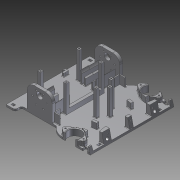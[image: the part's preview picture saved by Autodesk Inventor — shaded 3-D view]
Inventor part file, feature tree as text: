
AUTODESK INVENTOR PART (.ipt)
format: ipt  version: 2011 SP2 (Build 150309200, 309)  size: 1,286,144 bytes
history: native  units: mm
features: extrude x37, sketch x23, projected_geometry x15, fillet x14, mirror x3, plane x1, chamfer x1, hole x1
ambient origin geometry x8: Origin, YZ Plane, XZ Plane, XY Plane, X Axis, Y Axis, Z Axis, Center Point
feature tree (95):
  sketch  "Sketch1"  dims[d0=200.0mm d1=200.0mm]
  extrude  "Extrusion3"  Depth=200.0mm
  extrude  "Extrusion4"  Depth=10.5mm
  extrude  "Extrusion5"  Depth=6.5mm
  extrude  "Extrusion6"  Depth=53.3mm
  extrude  "Extrusion7"  Depth=26.65mm
  sketch  "Sketch4"  dims[d6=6.5mm d8=53.3mm]
  extrude  "Extrusion8"  Depth=5.0mm
  extrude  "Extrusion9"  Depth=5.0mm
  extrude  "Extrusion10"  Depth=4.6mm
  plane  "Work Plane1"
  mirror  "Mirror1"
  sketch  "Sketch9"  dims[d9=53.3mm d10=26.65mm]
  sketch  "Sketch10"  dims[d11=26.65mm d13=5.0mm]
  extrude  "Extrusion16"  Depth=8.0mm
  extrude  "Extrusion17"  Depth=8.0mm
  extrude  "Extrusion18"  Depth=138.0mm
  extrude  "Extrusion19"  Depth=3.0mm
  extrude  "Extrusion20"  Depth=12.061mm
  extrude  "Extrusion21"  Depth=4.0mm TaperAngle=0.0deg
  extrude  "Extrusion22"  Depth=55.0mm TaperAngle=0.0deg
  sketch  "Sketch13"  dims[d18=4.6mm d19=8.0mm]
  extrude  "Extrusion26"  Depth=38.0mm
  extrude  "Extrusion27"  Depth=7.0mm
  extrude  "Extrusion30"  Depth=15.5mm
  extrude  "Extrusion32"  Depth=55.0mm TaperAngle=0.0deg
  extrude  "Extrusion33"  Depth=2.0mm
  extrude  "Extrusion34"  Depth=3.9mm
  chamfer  "Chamfer2"  Distance=55.0mm
  fillet  "Fillet1"  Radius=36.8mm
  extrude  "Extrusion35"  Depth=40.0mm TaperAngle=0.0deg
  extrude  "Extrusion36"  Depth=23.0mm TaperAngle=0.0deg
  sketch  "Sketch21"  dims[d41=6.6mm d42=1.5mm d49=12.061mm]
  extrude  "Extrusion37"  Depth=2.8mm
  extrude  "Extrusion39"  Depth=2.8mm
  extrude  "Extrusion40"  Depth=2.8mm
  fillet  "Fillet2"  Radius=2.8mm
  sketch  "Sketch28"  dims[d64=13.0mm d65=38.0mm]
  extrude  "Extrusion48"  Depth=32.757mm
  extrude  "Extrusion49"  Depth=32.757mm
  extrude  "Extrusion42"  Depth=80.957mm
  extrude  "Extrusion44"  Depth=80.957mm
  fillet  "Fillet4"  Radius=27.264mm
  mirror  "Mirror3"
  fillet  "Fillet3"  Radius=20.564mm
  extrude  "Extrusion45"  Depth=34.936mm
  sketch  "Sketch30"  dims[d68=3.0mm d69=15.5mm]
  extrude  "Extrusion46"  Depth=35.936mm
  extrude  "Extrusion47"  Depth=2.0mm
  hole  "Hole1"  [1 undecoded]
  fillet  "Fillet5"  Radius=11.0mm
  fillet  "Fillet6"  Radius=2.0mm
  fillet  "Fillet7"  Radius=11.0mm
  fillet  "Fillet8"  Radius=11.0mm
  fillet  "Fillet9"  Radius=2.0mm
  fillet  "Fillet10"  Radius=2.0mm
  fillet  "Fillet11"  Radius=6.0mm
  fillet  "Fillet12"  Radius=6.0mm
  extrude  "Extrusion50"  Depth=6.0mm
  extrude  "Extrusion51"  Depth=6.0mm
  extrude  "Extrusion52"  Depth=3.0mm
  fillet  "Fillet13"  Radius=3.0mm
  fillet  "Fillet14"  Radius=3.0mm
  extrude  "Extrusion53"  Depth=3.0mm
  mirror  "Mirror4"
  sketch  "Sketch2"  dims[d2=10.5mm d3=10.5mm]
  sketch  "Sketch3"  dims[d4=57.861mm d5=6.5mm]
  projected_geometry  "Projected Loop1"
  projected_geometry  "Projected Loop7"
  sketch  "Sketch11"  dims[d14=5.0mm d15=5.0mm]
  sketch  "Sketch12"  dims[d16=6.35mm d17=4.6mm]
  projected_geometry  "Projected Loop8"
  sketch  "Sketch15"  dims[d20=5.0mm d21=8.0mm]
  projected_geometry  "Projected Loop9"
  sketch  "Sketch18"  dims[d22=5.0mm d25=138.0mm]
  projected_geometry  "Projected Loop11"
  sketch  "Sketch20"  dims[d29=3.65mm d30=3.65mm d31=3.0mm d34=1.5mm d37=3.0mm d38=5.0mm]
  projected_geometry  "Projected Loop12"
  sketch  "Sketch25"  dims[d50=5.0mm d58=4.0mm d59=0.0mm]
  sketch  "Sketch27"  dims[d60=11.0mm d61=0.0mm d62=55.0mm d63=0.0mm]
  projected_geometry  "Projected Loop16"
  sketch  "Sketch29"  dims[d66=36.8mm d67=7.0mm]
  sketch  "Sketch31"  dims[d70=60.0mm d72=360.0deg d74=55.0mm d75=0.0mm]
  projected_geometry  "Projected Loop17"
  projected_geometry  "Projected Loop18"
  projected_geometry  "Projected Loop19"
  projected_geometry  "Projected Loop20"
  projected_geometry  "Projected Loop21"
  projected_geometry  "Projected Loop22"
  projected_geometry  "Projected Loop23"
  sketch  "Sketch32"  dims[d76=2.0mm d77=2.0mm]
  sketch  "Sketch33"  dims[d78=3.9mm d79=3.9mm d80=55.0mm d81=0.0mm d82=36.8mm]
  sketch  "Sketch34"  dims[d83=36.0mm d84=40.0mm d85=0.0mm]
  sketch  "Sketch35"  dims[d86=40.0mm d87=0.0mm d88=23.0mm d89=0.0mm d119=2.8mm d120=2.8mm d121=2.8mm d122=2.8mm d135=32.757mm d136=32.757mm d137=80.957mm d138=80.957mm d139=27.264mm d140=20.564mm d141=34.936mm d142=35.936mm d143=2.0mm d144=11.0mm d145=11.0mm d146=2.0mm d147=11.0mm d148=11.0mm d149=2.0mm d150=2.0mm d155=6.0mm d156=6.0mm d157=6.0mm d158=6.0mm d159=3.0mm d160=3.0mm d161=3.0mm d162=3.0mm d163=6.0mm d164=6.0mm d165=3.0mm d166=3.0mm d167=6.0mm d168=6.0mm d169=3.0mm d170=3.0mm d181=3.0mm d182=3.5mm d184=0.0mm d185=0.0mm d186=200.0mm d187=0.0mm d188=200.0mm d189=0.0mm d190=58.0mm d191=0.0mm d192=18.0mm d193=0.0mm d194=40.0mm d195=0.0mm d196=1.570796mm d197=1.570796mm d198=220.0mm d199=220.0mm d200=10.0mm d201=10.0mm d202=5.0mm d203=7.0mm d204=0.0mm d205=0.0mm d215=32.1mm d231=5.0mm d233=12.0mm d234=0.0mm d239=20.0mm d240=0.0mm d256=6.0mm d257=167.0mm d258=6.2mm d259=6.0mm d260=0.0mm d262=22.75mm d266=10.0mm d267=38.9mm d268=5.5mm d269=32.1mm d272=10.0mm d273=12.2mm d276=12.0mm d277=0.0mm d278=28.5mm d279=10.3mm d280=0.0mm d281=5.0mm d282=0.0mm d283=0.5mm d284=5.3mm d285=45.0deg d286=1.0mm d287=5.0mm d288=0.0mm d289=3.0mm d290=3.0mm d291=10.0mm d292=0.0mm d293=6.35mm d294=4.6mm d295=2.0mm d296=3.0mm d297=10.0mm d298=0.0mm d306=41.0mm d307=0.0mm d308=6.0mm d309=6.0mm d310=2.575mm d311=2.575mm d312=2.0mm d313=2.0mm d315=8.956377mm d316=161.0mm d317=10.0mm d318=7.0mm d319=0.0mm d320=32.5mm d335=32.5mm d336=7.0mm d337=12.0mm d338=9.25mm d339=-0.872665mm d343=1.0mm d344=9.25mm d345=-0.872665mm d346=8.0mm d347=4.0mm d348=10.0mm d349=20.0mm d350=0.0mm d351=179.0mm d352=0.0mm d353=179.0mm d354=0.0mm d355=1.5mm d356=3.5mm d357=3.5mm d358=89.5mm d359=89.5mm d360=5.0mm d361=17.5mm d362=2.0mm d363=6.0mm d364=3.0mm d365=2.0mm d366=90.0deg d367=12.0mm d368=0.0mm d369=6.0mm d370=6.0mm d371=6.0mm d372=6.0mm d373=6.0mm d376=6.0mm d377=2.5mm d378=2.5mm d379=2.5mm d380=3.0mm d382=3.0mm d383=3.0mm d384=3.0mm d386=55.0mm d387=0.0mm d388=40.0mm d389=0.0mm d390=26.0mm d391=69.0mm d392=48.0mm d393=3.0mm d394=13.0mm d395=13.0mm d396=3.0mm d397=1.0mm d398=0.5mm d399=0.5mm d400=1.0mm d401=0.5mm d402=1.0mm d403=15.0mm d404=1.0mm d405=10.0mm d406=0.0mm d407=10.0mm d408=0.0mm d409=30.25mm d410=30.25mm d411=33.0mm d412=33.0mm d413=4.0mm d414=7.0mm d415=7.0mm d416=4.0mm d419=7.15mm d420=7.15mm d421=0.0mm d422=1.8mm d423=1.8mm d424=2.0mm d425=4.0mm d426=69.0mm d427=10.0mm d428=0.0mm d429=2.0mm d430=1.0mm d431=10.0mm d432=0.0mm]
  projected_geometry  "Projected Loop24"
note: 1 required parameter value undecoded (feature->parameter linkage not recoverable at this tier; creation-order binding heuristic only, values carry confidence <= 0.55)
